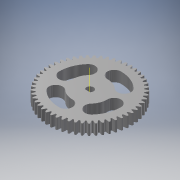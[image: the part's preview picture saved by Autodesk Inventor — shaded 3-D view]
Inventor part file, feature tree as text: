
AUTODESK INVENTOR PART (.ipt)
format: ipt  version: 2017 (Build 210142000, 142)  size: 553,984 bytes
history: native  units: mm (DEFAULTED — no unit token found)
features: other x4, sketch x4, extrude x3, plane x3, fillet x1, projected_geometry x1
ambient origin geometry x8: Origin, YZ Plane, XZ Plane, XY Plane, X Axis, Y Axis, Z Axis, Center Point
bodies: Solid1 (feature_tree)
feature tree (16):
  extrude  "Extrusion1"  Depth=8.0mm TaperAngle=0.0deg
  plane  "Work Plane2"
  plane  "Work Plane8"
  plane  "Work Plane9"
  other  "Spur Gear"
  extrude  "Extrusion2"  Depth=10.0mm TaperAngle=0.0deg
  other  "Work Axis1"
  extrude  "Extrusion3"  Depth=0.592753mm TaperAngle=0.0deg
  fillet  "Fillet1"  [1 undecoded]
  sketch  "Sketch1"  dims[d0=62.625mm d1=8.0mm d2=0.0mm]
  sketch  "Sketch2"  dims[d3=60.162162mm d4=10.0mm d5=0.0mm]
  other  "Srf1"
  sketch  "Sketch3"  dims[d16=42.0mm d17=0.0mm d34=0.592753mm d39=0.0mm]
  sketch  "Sketch4"  dims[d41=0.0mm d43=42.0mm d46=42.0mm d47=0.0mm d48=0.0mm d49=17.0mm d50=0.0mm d51=5.3mm d52=4.5mm d53=12.0mm d54=7.0mm d55=0.0mm d56=2.0mm d57=10.0mm d58=40.0mm d60=360.0deg]
  projected_geometry  "Projected Loop1"
  other  "Pitch Diameter"
note: 1 required parameter value undecoded (feature->parameter linkage not recoverable at this tier; creation-order binding heuristic only, values carry confidence <= 0.55)
